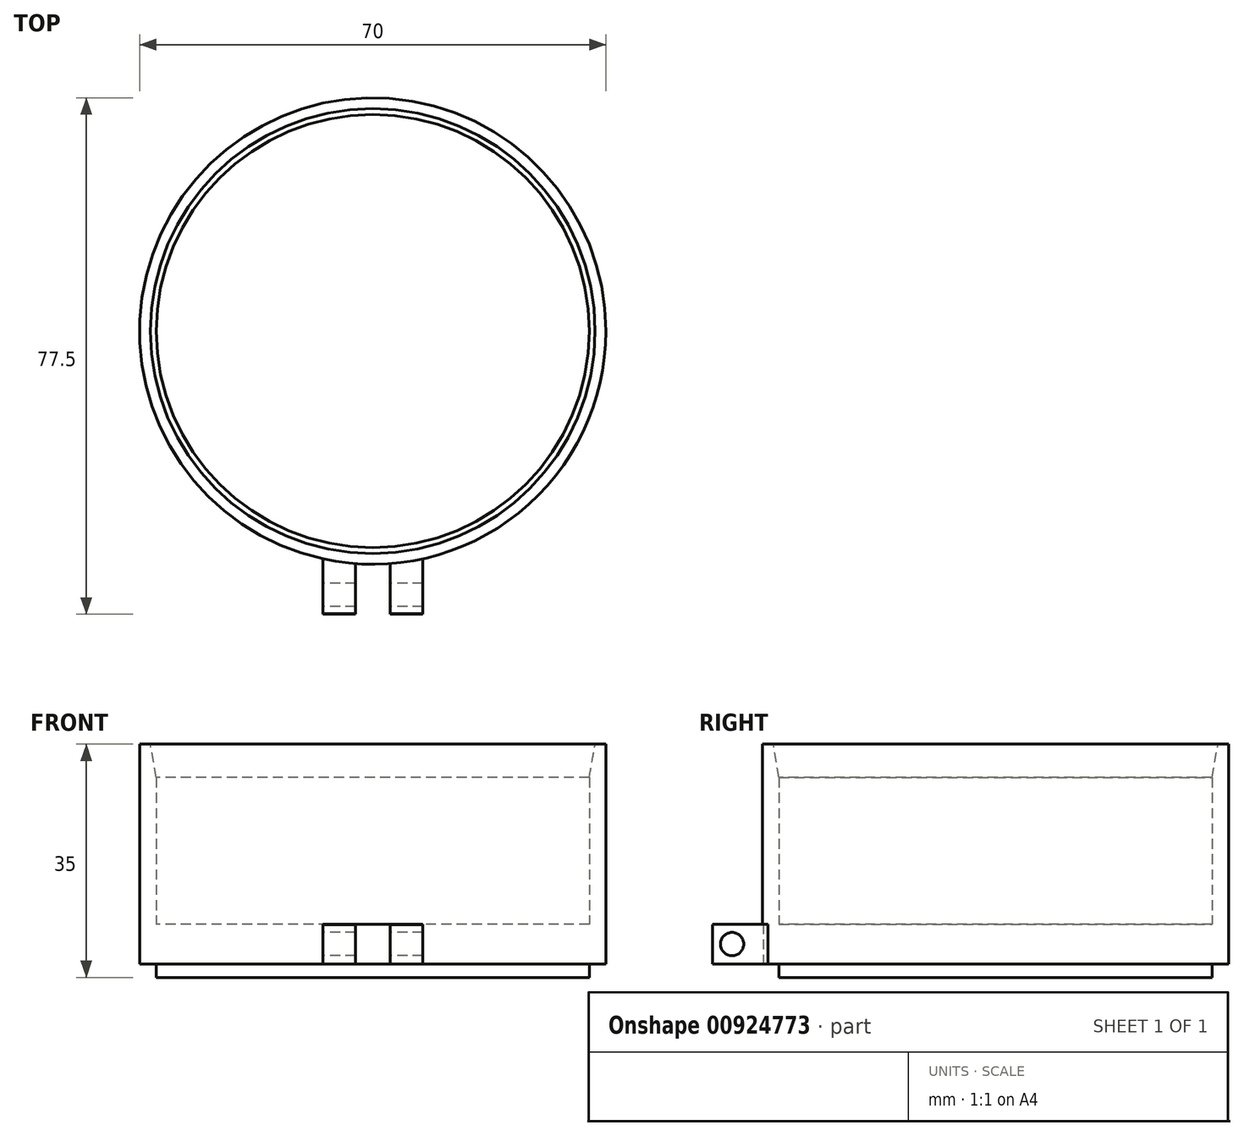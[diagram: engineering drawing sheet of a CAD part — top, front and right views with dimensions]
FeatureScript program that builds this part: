
annotation { "Feature Type Name" : "Feature", "Feature Type Description" : "" }
export const myFeature = defineFeature(function(context is Context, id is Id, definition is map)
    precondition{}
    {
        {
            var Q0;
            Q0=qCreatedBy(makeId("Top.planeOp"),FACE);
            var sketch = newSketch(context, id + "F0", { "sketchPlane" : qUnion([Q0])});
            skCircle(sketch, "E0", {"center": v(0, 0) * mm, "radius": 32.5 * mm});
            skCircle(sketch, "E1", {"center": v(0, 0) * mm, "radius": 35 * mm});
            skSolve(sketch);
        }
        {
            var Q0;
            Q0=makeQuery(id+"F0.imprint","IMPRINT",FACE,{"disambiguationData":[TD([[makeQuery(id+"F0.imprint","IMPRINT",EDGE,{"derivedFrom":sQuery(id+"F0.wireOp",EDGE,"E0")}),-1.0]])]});
            extrude(context, id + "F1", {"entities" : qUnion([Q0]), "depth" : 30 * mm, "offsetDistance" : 25 * mm});
        }
        {
            var Q0;
            Q0=makeQuery(id+"F1.opExtrude","CAP_FACE",FACE,{"disambiguationData":[OSD([sQuery(id+"F0.wireOp",EDGE,"E0"),sQuery(id+"F0.wireOp",EDGE,"E1")])],"isStart":true});
            var sketch = newSketch(context, id + "F2", { "sketchPlane" : qUnion([Q0])});
            skCircle(sketch, "E2", {"center": v(0, 0) * mm, "radius": 35 * mm});
            skCircle(sketch, "E3", {"center": v(0, 0) * mm, "radius": 32.5 * mm});
            skSolve(sketch);
        }
        {
            var Q0;
            Q0=makeQuery(id+"F2.imprint","IMPRINT",FACE,{"disambiguationData":[TD([[makeQuery(id+"F2.imprint","IMPRINT",EDGE,{"derivedFrom":sQuery(id+"F2.wireOp",EDGE,"E3")}),-1.0]])]});
            extrude(context, id + "F3", {"entities" : qUnion([Q0]), "depth" : 5 * mm, "offsetDistance" : 25 * mm});
        }
        {
            var Q0;
            Q0=makeQuery(id+"F1.opExtrude","CAP_FACE",FACE,{"disambiguationData":[OSD([sQuery(id+"F0.wireOp",EDGE,"E0"),sQuery(id+"F0.wireOp",EDGE,"E1")])],"isStart":true});
            extrude(context, id + "F4", {"entities" : qUnion([Q0]), "depth" : 3 * mm, "offsetDistance" : 25 * mm});
        }
        {
            var Q0;
            Q0=makeQuery(id+"F1.opExtrude","CAP_EDGE",EDGE,{"disambiguationData":[OSD([sQuery(id+"F0.wireOp",EDGE,"E0")])],"isStart":false});
            chamfer(context, id + "F5", {"entities" : qUnion([Q0]), "chamferType" : ChamferType.OFFSET_ANGLE, "width" : 5 * mm, "oppositeDirection" : false, "angle" : 10 * degree, "tangentPropagation" : true});
        }
        {
            var Q0;
            Q0=qCreatedBy(makeId("Top.planeOp"),FACE);
            var sketch = newSketch(context, id + "F6", { "sketchPlane" : qUnion([Q0])});
            skLineSegment(sketch, "E4.bottom", {"start": v(7.5, -42.5) * mm, "end": v(-7.5, -42.5) * mm});
            skLineSegment(sketch, "E4.left", {"start": v(7.5, -42.5) * mm, "end": v(7.5, -21.96) * mm});
            skLineSegment(sketch, "E4.right", {"start": v(-7.5, -42.5) * mm, "end": v(-7.5, -21.96) * mm});
            skPoint(sketch, "E4.middle", {"position": v(0, 0) * mm});
            skLineSegment(sketch, "E5", {"start": v(7.5, -21.96) * mm, "end": v(-7.5, -21.96) * mm});
            skPoint(sketch, "E4.top.start.orphan", {"position": v(7.5, 42.5) * mm});
            skPoint(sketch, "E6.orphan", {"position": v(-7.5, 42.5) * mm});
            skSolve(sketch);
        }
        {
            var Q0;
            Q0=makeQuery(id+"F6.imprint","IMPRINT",FACE,{"disambiguationData":[TD([[makeQuery(id+"F6.imprint","IMPRINT",EDGE,{"derivedFrom":sQuery(id+"F6.wireOp",EDGE,"E4.bottom")}),-1.0]])]});
            extrude(context, id + "F7", {"entities" : qUnion([Q0]), "operationType" : NewBodyOperationType.ADD, "oppositeDirection" : true, "depth" : 3 * mm, "offsetDistance" : 25 * mm});
        }
        {
            var Q0;
            {var subQ0=sQuery(id+"F6.wireOp",EDGE,"E4.bottom");var subQ2=sQuery(id+"F6.wireOp",EDGE,"E4.left");var subQ3=sQuery(id+"F6.wireOp",EDGE,"E4.right");Q0=makeQuery(id+"F7.boolean.opBoolean","SPLIT",FACE,{"disambiguationData":[TD([makeQuery(id+"F7.opExtrude","SWEPT_FACE",FACE,{"disambiguationData":[OSD([subQ0])]})])],"derivedFrom":makeQuery(id+"F7.opExtrude","CAP_FACE",FACE,{"disambiguationData":[OSD([subQ0,sQuery(id+"F6.wireOp",EDGE,"E4.top"),subQ2,subQ3])],"isStart":true})});}
            extrude(context, id + "F8", {"entities" : qUnion([Q0]), "operationType" : NewBodyOperationType.ADD, "depth" : 3 * mm, "offsetDistance" : 25 * mm});
        }
        {
            var Q0;
            {var subQ0=sQuery(id+"F6.wireOp",EDGE,"E4.bottom");Q0=makeQuery(id+"F8.boolean.opBoolean","MERGE",FACE,{"derivedFrom":[makeQuery(id+"F7.opExtrude","SWEPT_FACE",FACE,{"disambiguationData":[OSD([subQ0])]}),makeQuery(id+"F8.opExtrude","SWEPT_FACE",FACE,{"disambiguationData":[OSD([subQ0])]})]});}
            var sketch = newSketch(context, id + "F9", { "sketchPlane" : qUnion([Q0])});
            skLineSegment(sketch, "E7.bottom", {"start": v(2.6, 3) * mm, "end": v(-2.6, 3) * mm});
            skLineSegment(sketch, "E7.top", {"start": v(2.6, -3) * mm, "end": v(-2.6, -3) * mm});
            skLineSegment(sketch, "E7.left", {"start": v(2.6, 3) * mm, "end": v(2.6, -3) * mm});
            skLineSegment(sketch, "E7.right", {"start": v(-2.6, 3) * mm, "end": v(-2.6, -3) * mm});
            skPoint(sketch, "E7.middle", {"position": v(0, 0) * mm});
            skSolve(sketch);
        }
        {
            var Q0;
            Q0=makeQuery(id+"F9.imprint","IMPRINT",FACE,{"disambiguationData":[TD([[makeQuery(id+"F9.imprint","IMPRINT",EDGE,{"derivedFrom":sQuery(id+"F9.wireOp",EDGE,"E7.bottom")}),1.0]])]});
            extrude(context, id + "F10", {"entities" : qUnion([Q0]), "operationType" : NewBodyOperationType.REMOVE, "oppositeDirection" : true, "depth" : 7.6 * mm, "offsetDistance" : 25 * mm});
        }
        {
            var Q0;
            {var subQ0=sQuery(id+"F0.wireOp",EDGE,"E1");Q0=makeQuery(id+"F10.boolean.opBoolean","SPLIT",EDGE,{"disambiguationData":[topologyDisambiguationEdgeConnected([makeQuery(id+"F1.opExtrude","SWEPT_FACE",FACE,{"disambiguationData":[OSD([subQ0])]}),makeQuery(id+"F4.opExtrude","SWEPT_FACE",FACE,{"disambiguationData":[OSD([subQ0])]}),makeQuery(id+"F10.opExtrude","SWEPT_FACE",FACE,{"disambiguationData":[OSD([sQuery(id+"F9.wireOp",EDGE,"E7.bottom")])]})])],"derivedFrom":makeQuery(id+"F8.opExtrude","CAP_EDGE",EDGE,{"disambiguationData":[OSD([subQ0,sQuery(id+"F6.wireOp",EDGE,"E4.bottom"),sQuery(id+"F6.wireOp",EDGE,"E4.left"),sQuery(id+"F6.wireOp",EDGE,"E4.right"),sQuery(id+"F6.wireOp",EDGE,"E5")])],"isStart":false})});}
            chamfer(context, id + "F11", {"entities" : qUnion([Q0]), "width" : 0.1 * mm, "tangentPropagation" : true});
        }
        {
            var Q0;
            {var subQ0=sQuery(id+"F6.wireOp",EDGE,"E4.right");Q0=makeQuery(id+"F8.boolean.opBoolean","MERGE",FACE,{"derivedFrom":[makeQuery(id+"F7.opExtrude","SWEPT_FACE",FACE,{"disambiguationData":[OSD([subQ0])]}),makeQuery(id+"F8.opExtrude","SWEPT_FACE",FACE,{"disambiguationData":[OSD([subQ0])]})]});}
            var sketch = newSketch(context, id + "F12", { "sketchPlane" : qUnion([Q0])});
            skCircle(sketch, "E8", {"center": v(39.56, 0) * mm, "radius": 1.75 * mm});
            skSolve(sketch);
        }
        {
            var Q0;
            Q0=makeQuery(id+"F12.imprint","IMPRINT",FACE,{"disambiguationData":[TD([[makeQuery(id+"F12.imprint","IMPRINT",EDGE,{"derivedFrom":sQuery(id+"F12.wireOp",EDGE,"E8")}),1.0]])]});
            extrude(context, id + "F13", {"entities" : qUnion([Q0]), "operationType" : NewBodyOperationType.REMOVE, "oppositeDirection" : true, "depth" : 15 * mm, "offsetDistance" : 25 * mm});
        }
    });
